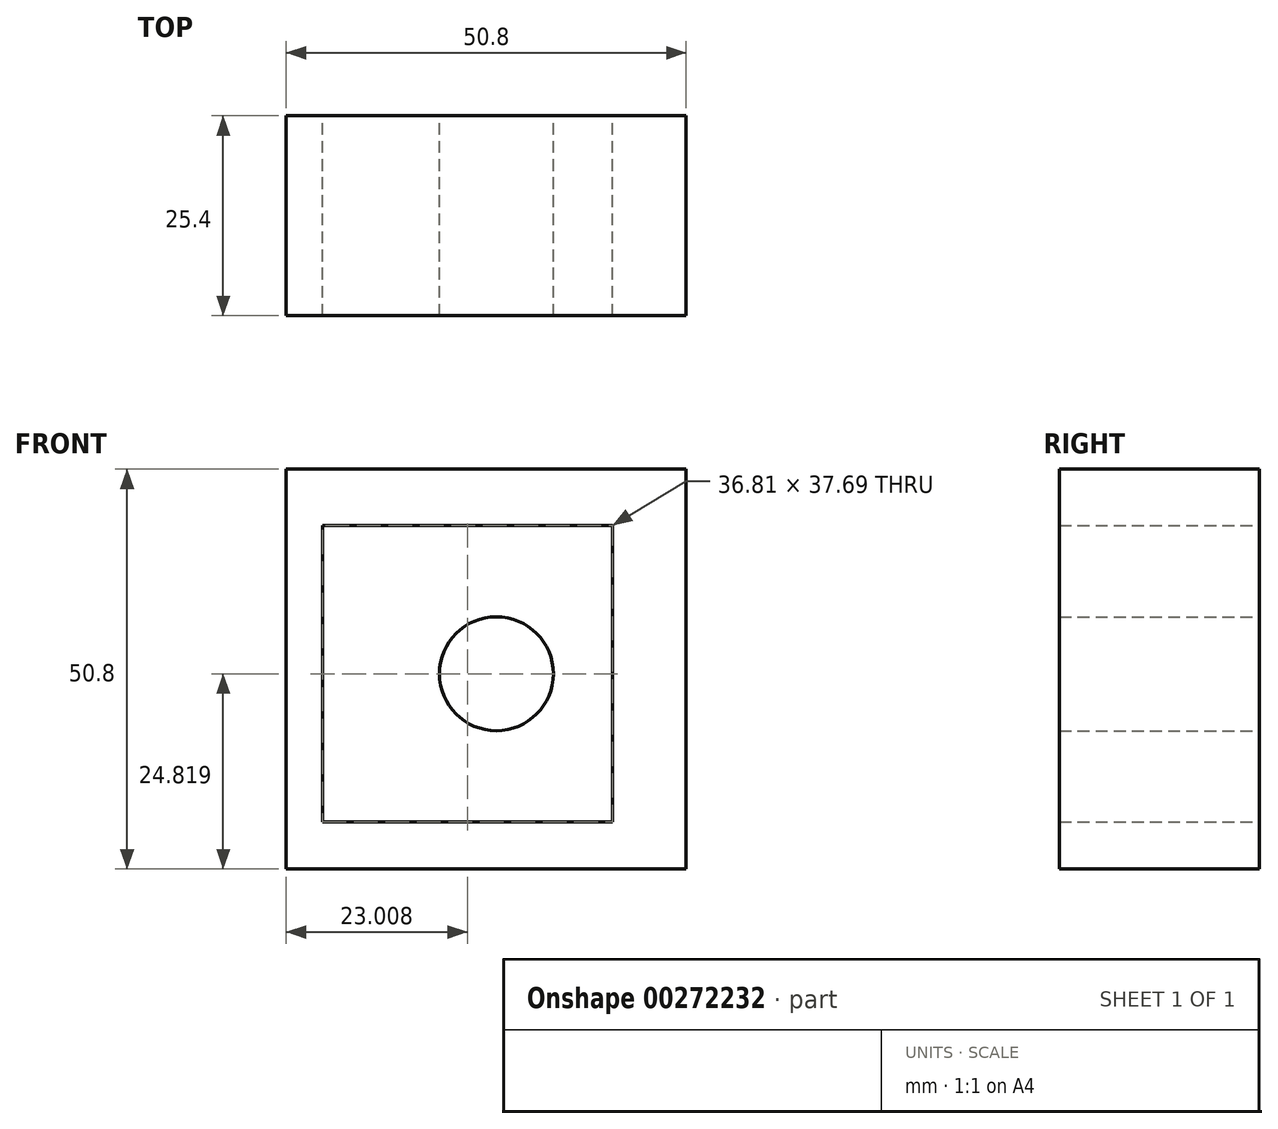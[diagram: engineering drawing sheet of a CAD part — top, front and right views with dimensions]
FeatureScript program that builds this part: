
annotation { "Feature Type Name" : "Feature", "Feature Type Description" : "" }
export const myFeature = defineFeature(function(context is Context, id is Id, definition is map)
    precondition{}
    {
        {
            var Q0;
            Q0=qCreatedBy(makeId("Front.planeOp"),FACE);
            var sketch = newSketch(context, id + "F0", { "sketchPlane" : qUnion([Q0])});
            skLineSegment(sketch, "E0", {"start": v(0, 0) * mm, "end": v(0, 50.8) * mm});
            skLineSegment(sketch, "E1", {"start": v(0, 50.8) * mm, "end": v(50.8, 50.8) * mm});
            skLineSegment(sketch, "E2", {"start": v(50.8, 50.8) * mm, "end": v(50.8, 0) * mm});
            skLineSegment(sketch, "E3", {"start": v(50.8, 0) * mm, "end": v(0, 0) * mm});
            skLineSegment(sketch, "E4.bottom", {"start": v(4.6, 43.66) * mm, "end": v(41.42, 43.66) * mm});
            skLineSegment(sketch, "E4.top", {"start": v(4.6, 5.97) * mm, "end": v(41.42, 5.97) * mm});
            skLineSegment(sketch, "E4.left", {"start": v(4.6, 43.66) * mm, "end": v(4.6, 5.97) * mm});
            skLineSegment(sketch, "E4.right", {"start": v(41.42, 43.66) * mm, "end": v(41.42, 5.97) * mm});
            skCircle(sketch, "E5", {"center": v(26.69, 24.82) * mm, "radius": 7.23 * mm});
            skPoint(sketch, "E5.centerSnap0", {"position": v(4.6, 24.82) * mm});
            skSolve(sketch);
        }
        {
            var Q0;
            Q0=makeQuery(id+"F0.imprint","IMPRINT",FACE,{"disambiguationData":[TD([[makeQuery(id+"F0.imprint","IMPRINT",EDGE,{"derivedFrom":sQuery(id+"F0.wireOp",EDGE,"E0")}),-1.0]])]});
            var Q1;
            Q1=makeQuery(id+"F0.imprint","IMPRINT",FACE,{"disambiguationData":[TD([[makeQuery(id+"F0.imprint","IMPRINT",EDGE,{"derivedFrom":sQuery(id+"F0.wireOp",EDGE,"E5")}),1.0]])]});
            extrude(context, id + "F1", {"entities" : qUnion([Q0, Q1]), "depth" : 25.4 * mm});
        }
    });
